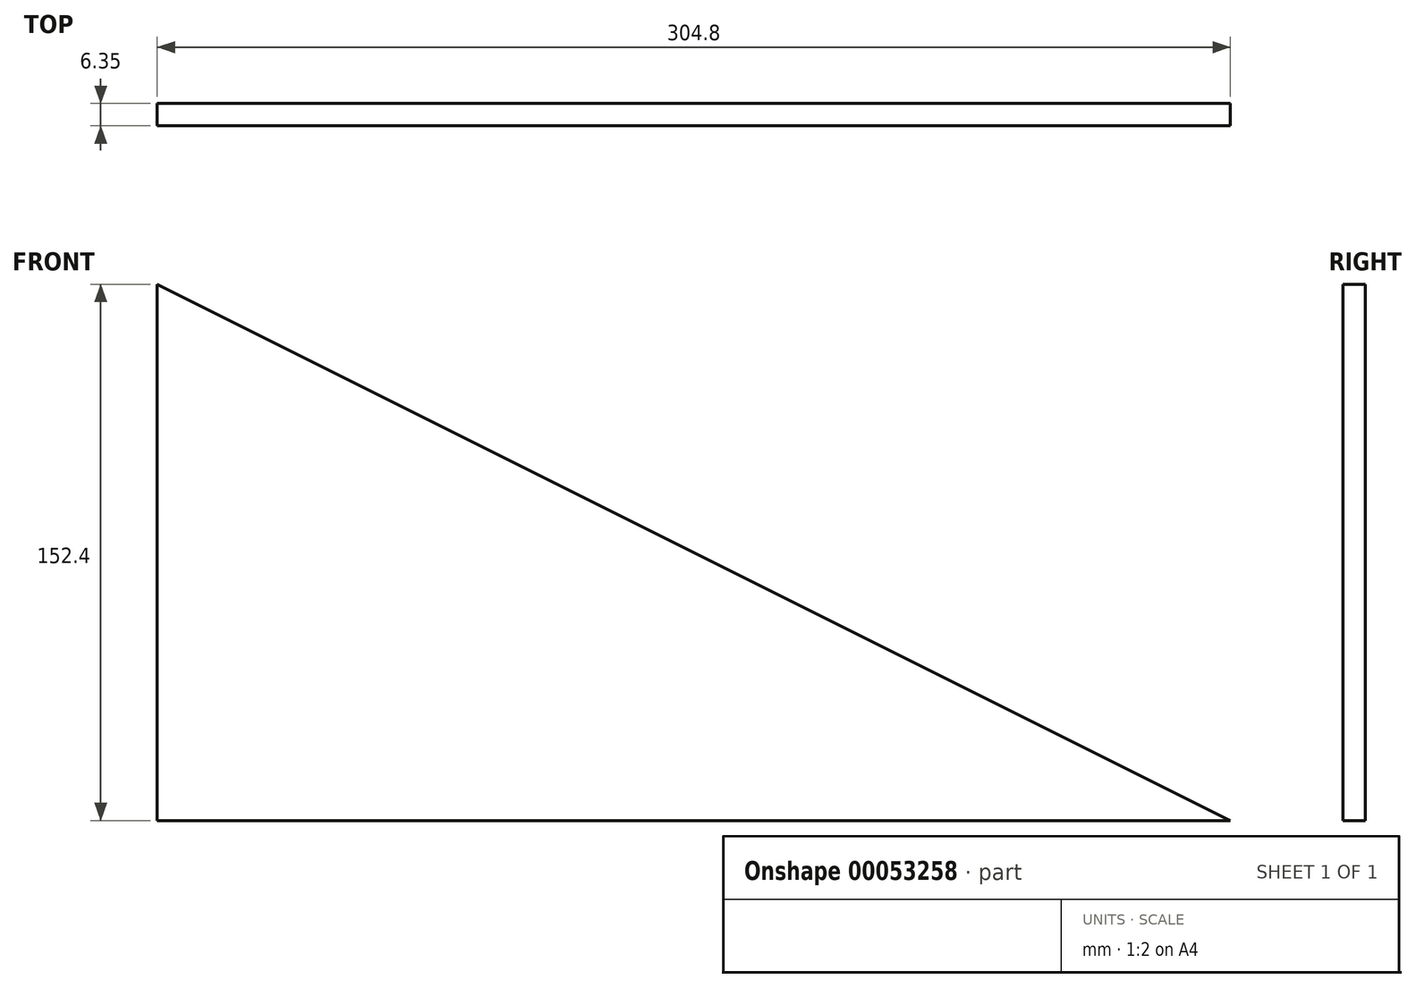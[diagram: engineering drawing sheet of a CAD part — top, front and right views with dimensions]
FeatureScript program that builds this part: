
annotation { "Feature Type Name" : "Feature", "Feature Type Description" : "" }
export const myFeature = defineFeature(function(context is Context, id is Id, definition is map)
    precondition{}
    {
        {
            var Q0;
            Q0=qCreatedBy(makeId("Front.planeOp"),FACE);
            var sketch = newSketch(context, id + "F0", { "sketchPlane" : qUnion([Q0])});
            skLineSegment(sketch, "E0", {"start": v(0, 0) * mm, "end": v(304.8, 0) * mm});
            skLineSegment(sketch, "E1", {"start": v(304.8, 0) * mm, "end": v(0, 152.4) * mm});
            skLineSegment(sketch, "E2", {"start": v(0, 152.4) * mm, "end": v(0, 0) * mm});
            skSolve(sketch);
        }
        {
            var Q0;
            Q0=makeQuery(id+"F0.imprint","IMPRINT",FACE,{"disambiguationData":[TD([[makeQuery(id+"F0.imprint","IMPRINT",EDGE,{"derivedFrom":sQuery(id+"F0.wireOp",EDGE,"E0")}),1.0]])]});
            extrude(context, id + "F1", {"entities" : qUnion([Q0]), "depth" : 6.35 * mm});
        }
    });
